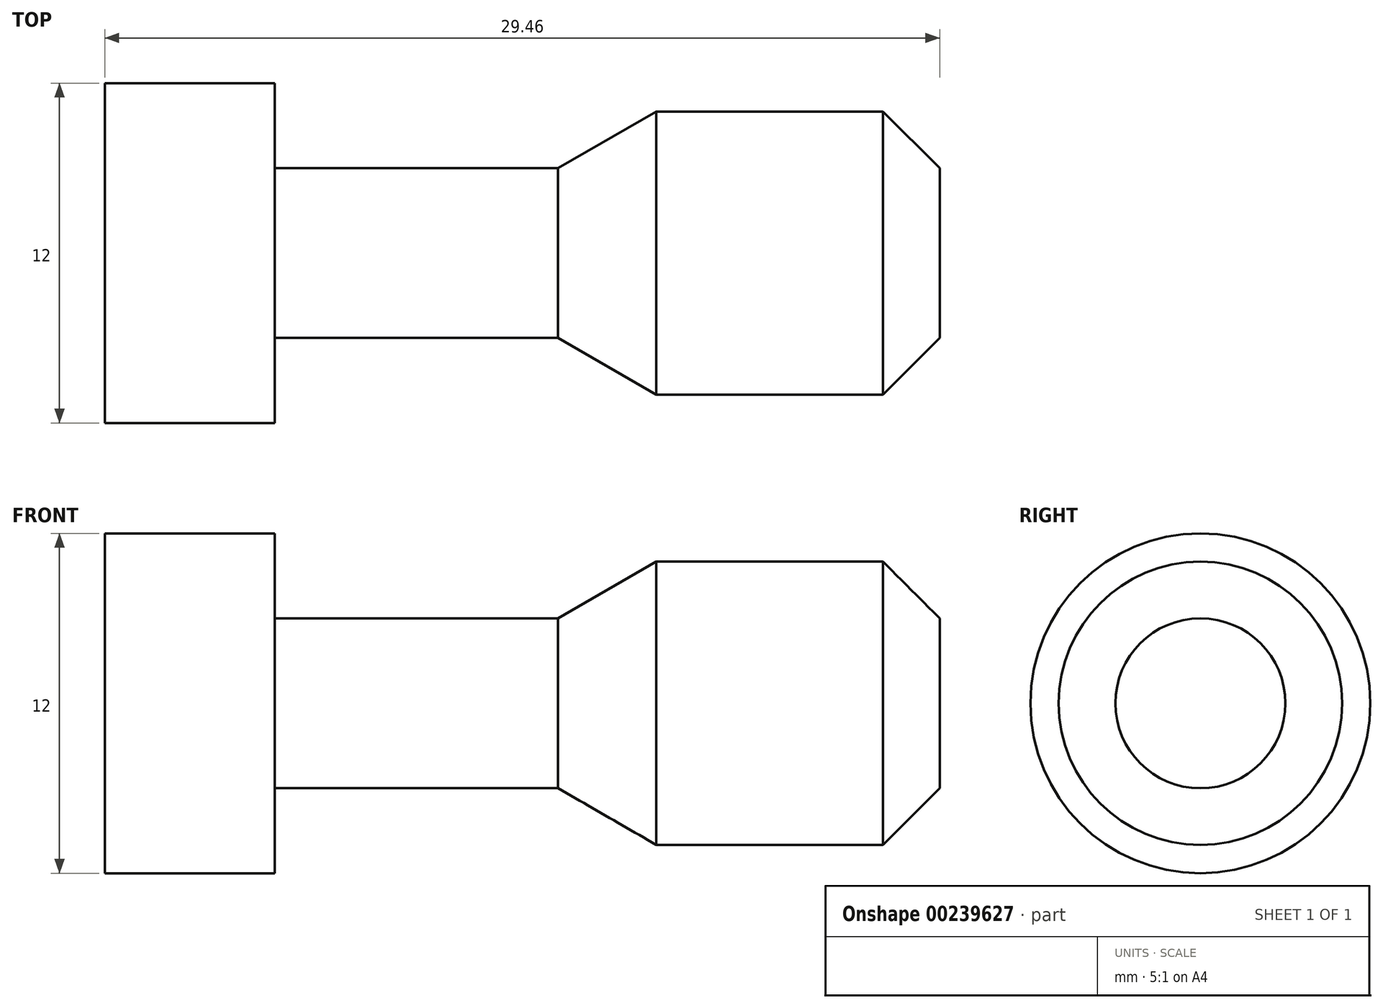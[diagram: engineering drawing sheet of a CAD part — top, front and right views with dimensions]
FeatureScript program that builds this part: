
annotation { "Feature Type Name" : "Feature", "Feature Type Description" : "" }
export const myFeature = defineFeature(function(context is Context, id is Id, definition is map)
    precondition{}
    {
        {
            var Q0;
            Q0=qCreatedBy(makeId("Front.planeOp"),FACE);
            var sketch = newSketch(context, id + "F0", { "sketchPlane" : qUnion([Q0])});
            skLineSegment(sketch, "E0.bottom", {"start": v(-10, 5) * mm, "end": v(0, 5) * mm});
            skLineSegment(sketch, "E0.top", {"start": v(-10, -5) * mm, "end": v(0, -5) * mm});
            skLineSegment(sketch, "E0.left", {"start": v(-10, 5) * mm, "end": v(-10, -5) * mm});
            skLineSegment(sketch, "E0.right", {"start": v(0, 5) * mm, "end": v(0, -5) * mm});
            skLineSegment(sketch, "E1", {"start": v(-10, 5) * mm, "end": v(-13.46, 3) * mm});
            skLineSegment(sketch, "E2.bottom", {"start": v(-13.46, 3) * mm, "end": v(-23.46, 3) * mm});
            skLineSegment(sketch, "E2.top", {"start": v(-13.46, -3) * mm, "end": v(-23.46, -3) * mm});
            skLineSegment(sketch, "E2.left", {"start": v(-13.46, 3) * mm, "end": v(-13.46, -3) * mm});
            skLineSegment(sketch, "E2.right", {"start": v(-23.46, 3) * mm, "end": v(-23.46, -3) * mm});
            skLineSegment(sketch, "E3", {"start": v(-13.46, -3) * mm, "end": v(-10, -5) * mm});
            skLineSegment(sketch, "E4", {"start": v(0, 0) * mm, "end": v(-29.68, 0) * mm});
            skLineSegment(sketch, "E5.bottom", {"start": v(-29.46, 6) * mm, "end": v(-23.46, 6) * mm});
            skLineSegment(sketch, "E5.top", {"start": v(-29.46, -6) * mm, "end": v(-23.46, -6) * mm});
            skLineSegment(sketch, "E5.left", {"start": v(-29.46, 6) * mm, "end": v(-29.46, -6) * mm});
            skLineSegment(sketch, "E5.right", {"start": v(-23.46, 6) * mm, "end": v(-23.46, -6) * mm});
            skSolve(sketch);
        }
        {
            var Q0;
            {var subQ0=sQuery(id+"F0.wireOp",EDGE,"E0.bottom");Q0=makeQuery(id+"F0.imprint","IMPRINT",FACE,{"disambiguationData":[TD([[makeQuery(id+"F0.imprint","IMPRINT",EDGE,{"derivedFrom":subQ0}),-1.0]])]});}
            var Q1;
            {var subQ0=sQuery(id+"F0.wireOp",EDGE,"E1");Q1=makeQuery(id+"F0.imprint","IMPRINT",FACE,{"disambiguationData":[TD([[makeQuery(id+"F0.imprint","IMPRINT",EDGE,{"derivedFrom":subQ0}),1.0]])]});}
            var Q2;
            {var subQ0=sQuery(id+"F0.wireOp",EDGE,"E2.bottom");Q2=makeQuery(id+"F0.imprint","IMPRINT",FACE,{"disambiguationData":[TD([[makeQuery(id+"F0.imprint","IMPRINT",EDGE,{"derivedFrom":subQ0}),1.0]])]});}
            var Q3;
            {var subQ2=sQuery(id+"F0.wireOp",EDGE,"E5.bottom");Q3=makeQuery(id+"F0.imprint","IMPRINT",FACE,{"disambiguationData":[TD([[makeQuery(id+"F0.imprint","IMPRINT",EDGE,{"derivedFrom":subQ2}),-1.0]])]});}
            var Q4;
            Q4=sQuery(id+"F0.wireOp",EDGE,"E5.left");
            var Q5;
            Q5=sQuery(id+"F0.wireOp",EDGE,"E4");
            revolve(context, id + "F1", {"entities" : qUnion([Q0, Q1, Q2, Q3]), "surfaceEntities" : qUnion([Q4]), "axis" : qUnion([Q5]), "revolveType" : RevolveType.FULL});
        }
        {
            var Q0;
            Q0=makeQuery(id+"F1.opRevolve","SWEPT_EDGE",EDGE,{"disambiguationData":[OSD([sQuery(id+"F0.wireOp",EDGE,"E0.bottom"),sQuery(id+"F0.wireOp",EDGE,"E0.right")])]});
            chamfer(context, id + "F2", {"entities" : qUnion([Q0]), "width" : 2 * mm, "tangentPropagation" : true});
        }
    });
